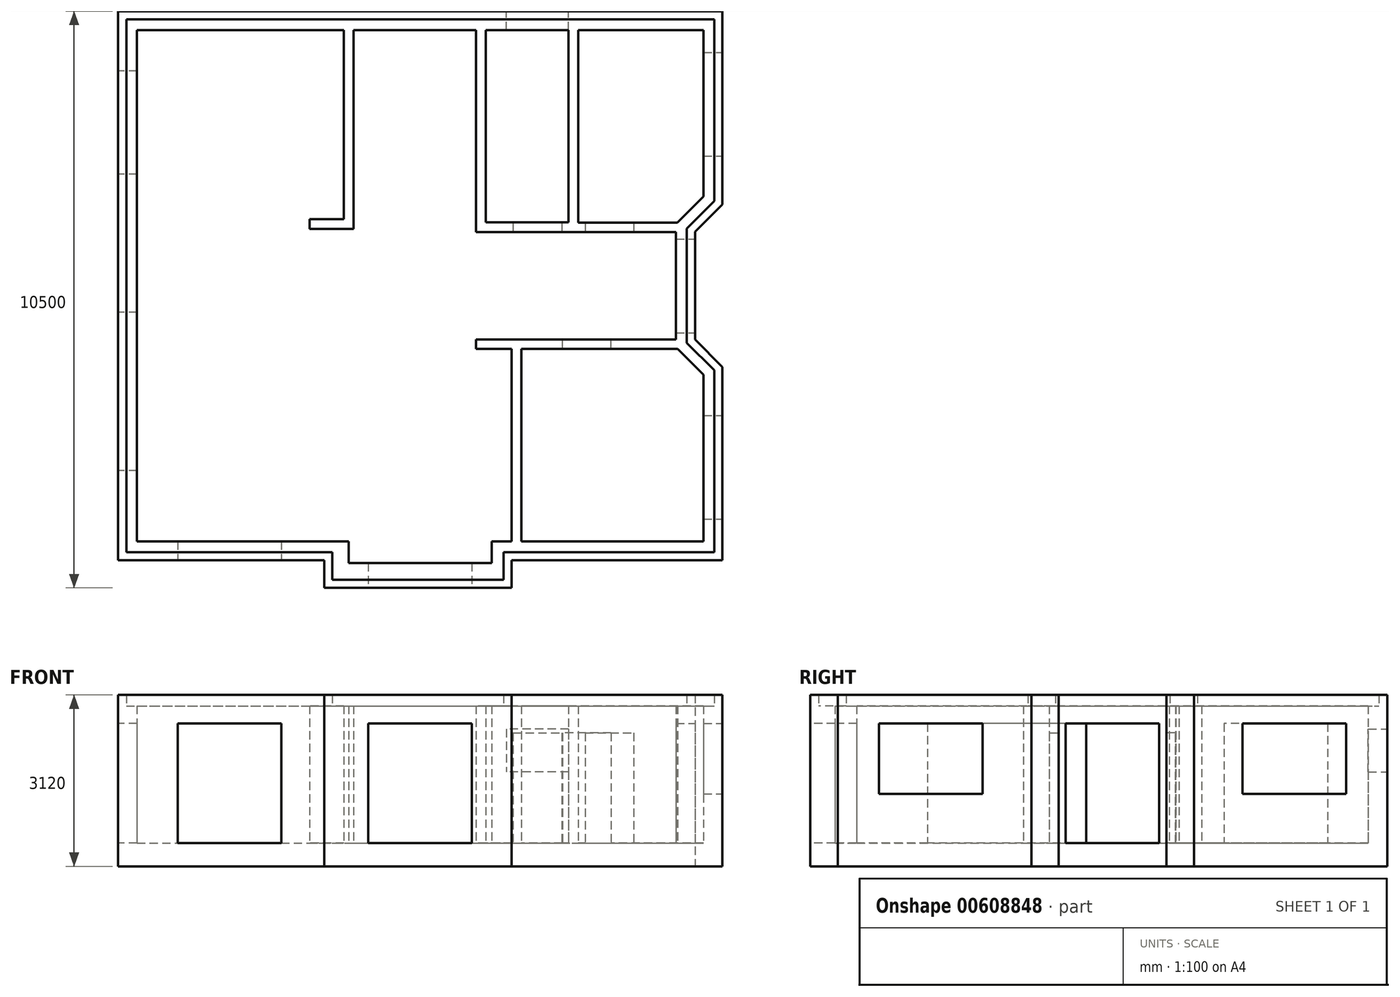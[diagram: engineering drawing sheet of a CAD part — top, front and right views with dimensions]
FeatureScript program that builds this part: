
annotation { "Feature Type Name" : "Feature", "Feature Type Description" : "" }
export const myFeature = defineFeature(function(context is Context, id is Id, definition is map)
    precondition{}
    {
        {
            var Q0;
            Q0=qCreatedBy(makeId("Top.planeOp"),FACE);
            var sketch = newSketch(context, id + "F0", { "sketchPlane" : qUnion([Q0])});
            skLineSegment(sketch, "E0.left", {"start": v(0, -10000) * mm, "end": v(0, 0) * mm});
            skLineSegment(sketch, "E1.bottom", {"start": v(345, -345) * mm, "end": v(4110, -345) * mm});
            skLineSegment(sketch, "E1.top", {"start": v(0, 0) * mm, "end": v(11000, 0) * mm});
            skLineSegment(sketch, "E2", {"start": v(345, -345) * mm, "end": v(345, -9655) * mm});
            skLineSegment(sketch, "E3", {"start": v(4110, -345) * mm, "end": v(4110, -3790) * mm});
            skLineSegment(sketch, "E4", {"start": v(4110, -3790) * mm, "end": v(3485, -3790) * mm});
            skLineSegment(sketch, "E5", {"start": v(3485, -3790) * mm, "end": v(3485, -3965) * mm});
            skLineSegment(sketch, "E6", {"start": v(3485, -3965) * mm, "end": v(4285, -3965) * mm});
            skLineSegment(sketch, "E7", {"start": v(4285, -3965) * mm, "end": v(4285, -345) * mm});
            skLineSegment(sketch, "E8.trimOffspring", {"start": v(4285, -345) * mm, "end": v(6515, -345) * mm});
            skLineSegment(sketch, "E9", {"start": v(6515, -345) * mm, "end": v(6515, -4020) * mm});
            skLineSegment(sketch, "E10", {"start": v(6515, -4020) * mm, "end": v(10155, -4020) * mm});
            skLineSegment(sketch, "E11", {"start": v(8200, -3845) * mm, "end": v(6690, -3845) * mm});
            skLineSegment(sketch, "E12", {"start": v(6690, -3845) * mm, "end": v(6690, -345) * mm});
            skLineSegment(sketch, "E13.trimOffspring", {"start": v(6690, -345) * mm, "end": v(8200, -345) * mm});
            skLineSegment(sketch, "E14", {"start": v(0, -10000) * mm, "end": v(3750, -10000) * mm});
            skLineSegment(sketch, "E15", {"start": v(3750, -10000) * mm, "end": v(3750, -10500) * mm});
            skLineSegment(sketch, "E16", {"start": v(3750, -10500) * mm, "end": v(7165, -10500) * mm});
            skLineSegment(sketch, "E17", {"start": v(7165, -10500) * mm, "end": v(7165, -10000) * mm});
            skLineSegment(sketch, "E18", {"start": v(7165, -10000) * mm, "end": v(11000, -10000) * mm});
            skLineSegment(sketch, "E19", {"start": v(11000, -10000) * mm, "end": v(11000, -6477.1) * mm});
            skLineSegment(sketch, "E20", {"start": v(10500, -5977.1) * mm, "end": v(10500, -4017.9) * mm});
            skLineSegment(sketch, "E21", {"start": v(10500, -4017.9) * mm, "end": v(11000, -3517.9) * mm});
            skLineSegment(sketch, "E22", {"start": v(11000, -3517.9) * mm, "end": v(11000, 0) * mm});
            skLineSegment(sketch, "E23", {"start": v(345, -9655) * mm, "end": v(4200, -9655) * mm});
            skLineSegment(sketch, "E24", {"start": v(4200, -9655) * mm, "end": v(4200, -10050) * mm});
            skLineSegment(sketch, "E25", {"start": v(4200, -10050) * mm, "end": v(6800, -10050) * mm});
            skLineSegment(sketch, "E26", {"start": v(6800, -10050) * mm, "end": v(6800, -9655) * mm});
            skLineSegment(sketch, "E27", {"start": v(6800, -9655) * mm, "end": v(7165, -9655) * mm});
            skLineSegment(sketch, "E28", {"start": v(10655, -9655) * mm, "end": v(10655, -6620) * mm});
            skLineSegment(sketch, "E29", {"start": v(10655, -6620) * mm, "end": v(10185, -6150) * mm});
            skLineSegment(sketch, "E30", {"start": v(10180, -3850) * mm, "end": v(10655, -3375) * mm});
            skLineSegment(sketch, "E31", {"start": v(10655, -3375) * mm, "end": v(10655, -345) * mm});
            skLineSegment(sketch, "E32", {"start": v(10185, -6150) * mm, "end": v(7340, -6150) * mm});
            skLineSegment(sketch, "E33", {"start": v(7340, -6150) * mm, "end": v(7340, -9655) * mm});
            skLineSegment(sketch, "E34", {"start": v(7165, -9655) * mm, "end": v(7165, -6150) * mm});
            skLineSegment(sketch, "E35", {"start": v(7165, -6150) * mm, "end": v(6515, -6150) * mm});
            skLineSegment(sketch, "E36", {"start": v(6515, -6150) * mm, "end": v(6515, -5975) * mm});
            skLineSegment(sketch, "E37", {"start": v(6515, -5975) * mm, "end": v(10155, -5975) * mm});
            skLineSegment(sketch, "E38", {"start": v(10155, -5975) * mm, "end": v(10155, -4020) * mm});
            skLineSegment(sketch, "E39.trimOffspring", {"start": v(7340, -9655) * mm, "end": v(10655, -9655) * mm});
            skLineSegment(sketch, "E40", {"start": v(10180, -3850) * mm, "end": v(8375, -3850) * mm});
            skLineSegment(sketch, "E41", {"start": v(8375, -3850) * mm, "end": v(8375, -345) * mm});
            skLineSegment(sketch, "E42", {"start": v(8200, -345) * mm, "end": v(8200, -3845) * mm});
            skLineSegment(sketch, "E43.trimOffspring", {"start": v(8375, -345) * mm, "end": v(10655, -345) * mm});
            skLineSegment(sketch, "E44", {"start": v(10500, -5977.1) * mm, "end": v(11000, -6477.1) * mm});
            skSolve(sketch);
        }
        {
            var Q0;
            Q0=makeQuery(id+"F0.imprint","IMPRINT",FACE,{"disambiguationData":[TD([[makeQuery(id+"F0.imprint","IMPRINT",EDGE,{"derivedFrom":sQuery(id+"F0.wireOp",EDGE,"E0.left")}),-1.0]])]});
            extrude(context, id + "F1", {"entities" : qUnion([Q0]), "depth" : 2500 * mm, "offsetDistance" : 25 * mm});
        }
        {
            var Q0;
            Q0=makeQuery(id+"F1.opExtrude","CAP_FACE",FACE,{"disambiguationData":[OSD([sQuery(id+"F0.wireOp",EDGE,"E0.left"),sQuery(id+"F0.wireOp",EDGE,"E1.bottom"),sQuery(id+"F0.wireOp",EDGE,"E1.top"),sQuery(id+"F0.wireOp",EDGE,"E2"),sQuery(id+"F0.wireOp",EDGE,"E3"),sQuery(id+"F0.wireOp",EDGE,"E4"),sQuery(id+"F0.wireOp",EDGE,"E5"),sQuery(id+"F0.wireOp",EDGE,"E6"),sQuery(id+"F0.wireOp",EDGE,"E7"),sQuery(id+"F0.wireOp",EDGE,"E8.trimOffspring"),sQuery(id+"F0.wireOp",EDGE,"E9"),sQuery(id+"F0.wireOp",EDGE,"E10"),sQuery(id+"F0.wireOp",EDGE,"E11"),sQuery(id+"F0.wireOp",EDGE,"E12"),sQuery(id+"F0.wireOp",EDGE,"E13.trimOffspring"),sQuery(id+"F0.wireOp",EDGE,"E14"),sQuery(id+"F0.wireOp",EDGE,"E15"),sQuery(id+"F0.wireOp",EDGE,"E16"),sQuery(id+"F0.wireOp",EDGE,"E17"),sQuery(id+"F0.wireOp",EDGE,"E18"),sQuery(id+"F0.wireOp",EDGE,"E19"),sQuery(id+"F0.wireOp",EDGE,"E20"),sQuery(id+"F0.wireOp",EDGE,"E21"),sQuery(id+"F0.wireOp",EDGE,"E22"),sQuery(id+"F0.wireOp",EDGE,"E23"),sQuery(id+"F0.wireOp",EDGE,"E24"),sQuery(id+"F0.wireOp",EDGE,"E25"),sQuery(id+"F0.wireOp",EDGE,"E26"),sQuery(id+"F0.wireOp",EDGE,"E27"),sQuery(id+"F0.wireOp",EDGE,"E28"),sQuery(id+"F0.wireOp",EDGE,"E29"),sQuery(id+"F0.wireOp",EDGE,"E30"),sQuery(id+"F0.wireOp",EDGE,"E31"),sQuery(id+"F0.wireOp",EDGE,"E32"),sQuery(id+"F0.wireOp",EDGE,"E33"),sQuery(id+"F0.wireOp",EDGE,"E34"),sQuery(id+"F0.wireOp",EDGE,"E35"),sQuery(id+"F0.wireOp",EDGE,"E36"),sQuery(id+"F0.wireOp",EDGE,"E37"),sQuery(id+"F0.wireOp",EDGE,"E38"),sQuery(id+"F0.wireOp",EDGE,"E39.trimOffspring"),sQuery(id+"F0.wireOp",EDGE,"E40"),sQuery(id+"F0.wireOp",EDGE,"E41"),sQuery(id+"F0.wireOp",EDGE,"E42"),sQuery(id+"F0.wireOp",EDGE,"E43.trimOffspring"),sQuery(id+"F0.wireOp",EDGE,"E44")])],"isStart":true});
            var sketch = newSketch(context, id + "F2", { "sketchPlane" : qUnion([Q0])});
            skLineSegment(sketch, "E45.0", {"start": v(0, 10000) * mm, "end": v(0, 0) * mm});
            skLineSegment(sketch, "E46.0", {"start": v(0, 0) * mm, "end": v(11000, 0) * mm});
            skLineSegment(sketch, "E47.0", {"start": v(11000, 3517.9) * mm, "end": v(11000, 0) * mm});
            skLineSegment(sketch, "E48.0", {"start": v(10500, 4017.9) * mm, "end": v(11000, 3517.9) * mm});
            skLineSegment(sketch, "E49.0", {"start": v(10500, 5977.1) * mm, "end": v(10500, 4017.9) * mm});
            skLineSegment(sketch, "E50.0", {"start": v(10500, 5977.1) * mm, "end": v(11000, 6477.1) * mm});
            skLineSegment(sketch, "E51.0", {"start": v(11000, 10000) * mm, "end": v(11000, 6477.1) * mm});
            skLineSegment(sketch, "E52.0", {"start": v(7165, 10000) * mm, "end": v(11000, 10000) * mm});
            skLineSegment(sketch, "E53.0", {"start": v(7165, 10500) * mm, "end": v(7165, 10000) * mm});
            skLineSegment(sketch, "E54.0", {"start": v(3750, 10500) * mm, "end": v(7165, 10500) * mm});
            skLineSegment(sketch, "E55.0", {"start": v(3750, 10000) * mm, "end": v(3750, 10500) * mm});
            skLineSegment(sketch, "E56.0", {"start": v(0, 10000) * mm, "end": v(3750, 10000) * mm});
            skSolve(sketch);
        }
        {
            var Q0;
            Q0 = qSketchRegion(id + "F2", true);
            extrude(context, id + "F3", {"entities" : qUnion([Q0]), "operationType" : NewBodyOperationType.ADD, "depth" : (250 + 170) * mm, "offsetDistance" : 25 * mm});
        }
        {
            var Q0;
            Q0=makeQuery(id+"F3.boolean.opBoolean","MERGE",FACE,{"derivedFrom":[makeQuery(id+"F1.opExtrude","SWEPT_FACE",FACE,{"disambiguationData":[OSD([sQuery(id+"F0.wireOp",EDGE,"E20")])]}),makeQuery(id+"F3.opExtrude","SWEPT_FACE",FACE,{"disambiguationData":[OSD([sQuery(id+"F2.wireOp",EDGE,"E49.0")])]})]});
            var sketch = newSketch(context, id + "F4", { "sketchPlane" : qUnion([Q0])});
            skLineSegment(sketch, "E57.bottom", {"start": v(-5855, 2180) * mm, "end": v(-4150, 2180) * mm});
            skLineSegment(sketch, "E57.top", {"start": v(-5855, 0) * mm, "end": v(-4150, 0) * mm});
            skLineSegment(sketch, "E57.left", {"start": v(-5855, 2180) * mm, "end": v(-5855, 0) * mm});
            skLineSegment(sketch, "E57.right", {"start": v(-4150, 2180) * mm, "end": v(-4150, 0) * mm});
            skSolve(sketch);
        }
        {
            var Q0;
            Q0 = qSketchRegion(id + "F4", true);
            extrude(context, id + "F5", {"entities" : qUnion([Q0]), "operationType" : NewBodyOperationType.REMOVE, "endBound" : BoundingType.UP_TO_NEXT, "oppositeDirection" : true, "depth" : 25 * mm, "offsetDistance" : 25 * mm});
        }
        {
            var Q0;
            Q0=makeQuery(id+"F1.opExtrude","SWEPT_FACE",FACE,{"disambiguationData":[OSD([sQuery(id+"F0.wireOp",EDGE,"E10")])]});
            var sketch = newSketch(context, id + "F6", { "sketchPlane" : qUnion([Q0])});
            skLineSegment(sketch, "E58.bottom", {"start": v(7190, 2010) * mm, "end": v(8075, 2010) * mm});
            skLineSegment(sketch, "E58.top", {"start": v(7190, 0) * mm, "end": v(8075, 0) * mm});
            skLineSegment(sketch, "E58.left", {"start": v(7190, 2010) * mm, "end": v(7190, 0) * mm});
            skLineSegment(sketch, "E58.right", {"start": v(8075, 2010) * mm, "end": v(8075, 0) * mm});
            skLineSegment(sketch, "E59.bottom", {"start": v(8500, 2010) * mm, "end": v(9385, 2010) * mm});
            skLineSegment(sketch, "E59.top", {"start": v(8500, 0) * mm, "end": v(9385, 0) * mm});
            skLineSegment(sketch, "E59.left", {"start": v(8500, 2010) * mm, "end": v(8500, 0) * mm});
            skLineSegment(sketch, "E59.right", {"start": v(9385, 2010) * mm, "end": v(9385, 0) * mm});
            skSolve(sketch);
        }
        {
            var Q0;
            Q0 = qSketchRegion(id + "F6", true);
            extrude(context, id + "F7", {"entities" : qUnion([Q0]), "operationType" : NewBodyOperationType.REMOVE, "endBound" : BoundingType.UP_TO_NEXT, "oppositeDirection" : true, "depth" : 25 * mm, "offsetDistance" : 25 * mm});
        }
        {
            var Q0;
            Q0=makeQuery(id+"F1.opExtrude","SWEPT_FACE",FACE,{"disambiguationData":[OSD([sQuery(id+"F0.wireOp",EDGE,"E37")])]});
            var sketch = newSketch(context, id + "F8", { "sketchPlane" : qUnion([Q0])});
            skLineSegment(sketch, "E60.bottom", {"start": v(-8975, 2010) * mm, "end": v(-8090, 2010) * mm});
            skLineSegment(sketch, "E60.top", {"start": v(-8975, 0) * mm, "end": v(-8090, 0) * mm});
            skLineSegment(sketch, "E60.left", {"start": v(-8975, 2010) * mm, "end": v(-8975, 0) * mm});
            skLineSegment(sketch, "E60.right", {"start": v(-8090, 2010) * mm, "end": v(-8090, 0) * mm});
            skSolve(sketch);
        }
        {
            var Q0;
            Q0 = qSketchRegion(id + "F8", true);
            extrude(context, id + "F9", {"entities" : qUnion([Q0]), "operationType" : NewBodyOperationType.REMOVE, "endBound" : BoundingType.UP_TO_NEXT, "oppositeDirection" : true, "depth" : 25 * mm, "offsetDistance" : 25 * mm});
        }
        {
            var Q0;
            Q0=makeQuery(id+"F3.boolean.opBoolean","MERGE",FACE,{"derivedFrom":[makeQuery(id+"F1.opExtrude","SWEPT_FACE",FACE,{"disambiguationData":[OSD([sQuery(id+"F0.wireOp",EDGE,"E0.left")])]}),makeQuery(id+"F3.opExtrude","SWEPT_FACE",FACE,{"disambiguationData":[OSD([sQuery(id+"F2.wireOp",EDGE,"E45.0")])]})]});
            var sketch = newSketch(context, id + "F10", { "sketchPlane" : qUnion([Q0])});
            skLineSegment(sketch, "E61.bottom", {"start": v(1085, 2180) * mm, "end": v(2970, 2180) * mm});
            skLineSegment(sketch, "E61.top", {"start": v(1085, 0) * mm, "end": v(2970, 0) * mm});
            skLineSegment(sketch, "E61.left", {"start": v(1085, 2180) * mm, "end": v(1085, 0) * mm});
            skLineSegment(sketch, "E61.right", {"start": v(2970, 2180) * mm, "end": v(2970, 0) * mm});
            skLineSegment(sketch, "E62.bottom", {"start": v(5480, 2180) * mm, "end": v(8365, 2180) * mm});
            skLineSegment(sketch, "E62.top", {"start": v(5480, 0) * mm, "end": v(8365, 0) * mm});
            skLineSegment(sketch, "E62.left", {"start": v(5480, 2180) * mm, "end": v(5480, 0) * mm});
            skLineSegment(sketch, "E62.right", {"start": v(8365, 2180) * mm, "end": v(8365, 0) * mm});
            skSolve(sketch);
        }
        {
            var Q0;
            Q0 = qSketchRegion(id + "F10", true);
            extrude(context, id + "F11", {"entities" : qUnion([Q0]), "operationType" : NewBodyOperationType.REMOVE, "endBound" : BoundingType.UP_TO_NEXT, "oppositeDirection" : true, "depth" : 25 * mm, "offsetDistance" : 25 * mm});
        }
        {
            var Q0;
            Q0=makeQuery(id+"F3.boolean.opBoolean","MERGE",FACE,{"derivedFrom":[makeQuery(id+"F1.opExtrude","SWEPT_FACE",FACE,{"disambiguationData":[OSD([sQuery(id+"F0.wireOp",EDGE,"E14")])]}),makeQuery(id+"F3.opExtrude","SWEPT_FACE",FACE,{"disambiguationData":[OSD([sQuery(id+"F2.wireOp",EDGE,"E56.0")])]})]});
            var sketch = newSketch(context, id + "F12", { "sketchPlane" : qUnion([Q0])});
            skLineSegment(sketch, "E63.bottom", {"start": v(1085, 2180) * mm, "end": v(2970, 2180) * mm});
            skLineSegment(sketch, "E63.top", {"start": v(1085, 0) * mm, "end": v(2970, 0) * mm});
            skLineSegment(sketch, "E63.left", {"start": v(1085, 2180) * mm, "end": v(1085, 0) * mm});
            skLineSegment(sketch, "E63.right", {"start": v(2970, 2180) * mm, "end": v(2970, 0) * mm});
            skSolve(sketch);
        }
        {
            var Q0;
            Q0=makeQuery(id+"F12.imprint","IMPRINT",FACE,{"disambiguationData":[TD([[makeQuery(id+"F12.imprint","IMPRINT",EDGE,{"derivedFrom":sQuery(id+"F12.wireOp",EDGE,"E63.bottom")}),-1.0]])]});
            extrude(context, id + "F13", {"entities" : qUnion([Q0]), "operationType" : NewBodyOperationType.REMOVE, "endBound" : BoundingType.UP_TO_NEXT, "oppositeDirection" : true, "depth" : 25 * mm, "offsetDistance" : 25 * mm});
        }
        {
            var Q0;
            Q0=makeQuery(id+"F3.boolean.opBoolean","MERGE",FACE,{"derivedFrom":[makeQuery(id+"F1.opExtrude","SWEPT_FACE",FACE,{"disambiguationData":[OSD([sQuery(id+"F0.wireOp",EDGE,"E16")])]}),makeQuery(id+"F3.opExtrude","SWEPT_FACE",FACE,{"disambiguationData":[OSD([sQuery(id+"F2.wireOp",EDGE,"E54.0")])]})]});
            var sketch = newSketch(context, id + "F14", { "sketchPlane" : qUnion([Q0])});
            skLineSegment(sketch, "E64.bottom", {"start": v(4555, 2180) * mm, "end": v(6440, 2180) * mm});
            skLineSegment(sketch, "E64.top", {"start": v(4555, 0) * mm, "end": v(6440, 0) * mm});
            skLineSegment(sketch, "E64.left", {"start": v(4555, 2180) * mm, "end": v(4555, 0) * mm});
            skLineSegment(sketch, "E64.right", {"start": v(6440, 2180) * mm, "end": v(6440, 0) * mm});
            skSolve(sketch);
        }
        {
            var Q0;
            Q0=makeQuery(id+"F14.imprint","IMPRINT",FACE,{"disambiguationData":[TD([[makeQuery(id+"F14.imprint","IMPRINT",EDGE,{"derivedFrom":sQuery(id+"F14.wireOp",EDGE,"E64.bottom")}),-1.0]])]});
            extrude(context, id + "F15", {"entities" : qUnion([Q0]), "operationType" : NewBodyOperationType.REMOVE, "endBound" : BoundingType.UP_TO_NEXT, "oppositeDirection" : true, "depth" : 25 * mm, "offsetDistance" : 25 * mm});
        }
        {
            var Q0;
            Q0=makeQuery(id+"F3.boolean.opBoolean","MERGE",FACE,{"derivedFrom":[makeQuery(id+"F1.opExtrude","SWEPT_FACE",FACE,{"disambiguationData":[OSD([sQuery(id+"F0.wireOp",EDGE,"E19")])]}),makeQuery(id+"F3.opExtrude","SWEPT_FACE",FACE,{"disambiguationData":[OSD([sQuery(id+"F2.wireOp",EDGE,"E51.0")])]})]});
            var sketch = newSketch(context, id + "F16", { "sketchPlane" : qUnion([Q0])});
            skLineSegment(sketch, "E65.bottom", {"start": v(-9250, 2180) * mm, "end": v(-7365, 2180) * mm});
            skLineSegment(sketch, "E65.top", {"start": v(-9250, 900) * mm, "end": v(-7365, 900) * mm});
            skLineSegment(sketch, "E65.left", {"start": v(-9250, 2180) * mm, "end": v(-9250, 900) * mm});
            skLineSegment(sketch, "E65.right", {"start": v(-7365, 2180) * mm, "end": v(-7365, 900) * mm});
            skLineSegment(sketch, "E66.bottom", {"start": v(-2635, 2180) * mm, "end": v(-750, 2180) * mm});
            skLineSegment(sketch, "E66.top", {"start": v(-2635, 900) * mm, "end": v(-750, 900) * mm});
            skLineSegment(sketch, "E66.left", {"start": v(-2635, 2180) * mm, "end": v(-2635, 900) * mm});
            skLineSegment(sketch, "E66.right", {"start": v(-750, 2180) * mm, "end": v(-750, 900) * mm});
            skSolve(sketch);
        }
        {
            var Q0;
            Q0=makeQuery(id+"F16.imprint","IMPRINT",FACE,{"disambiguationData":[TD([[makeQuery(id+"F16.imprint","IMPRINT",EDGE,{"derivedFrom":sQuery(id+"F16.wireOp",EDGE,"E65.bottom")}),-1.0]])]});
            var Q1;
            Q1=makeQuery(id+"F16.imprint","IMPRINT",FACE,{"disambiguationData":[TD([[makeQuery(id+"F16.imprint","IMPRINT",EDGE,{"derivedFrom":sQuery(id+"F16.wireOp",EDGE,"E66.bottom")}),-1.0]])]});
            extrude(context, id + "F17", {"entities" : qUnion([Q0, Q1]), "operationType" : NewBodyOperationType.REMOVE, "endBound" : BoundingType.UP_TO_NEXT, "oppositeDirection" : true, "depth" : 25 * mm, "offsetDistance" : 25 * mm});
        }
        {
            var Q0;
            Q0=makeQuery(id+"F3.boolean.opBoolean","MERGE",FACE,{"derivedFrom":[makeQuery(id+"F1.opExtrude","SWEPT_FACE",FACE,{"disambiguationData":[OSD([sQuery(id+"F0.wireOp",EDGE,"E1.top")])]}),makeQuery(id+"F3.opExtrude","SWEPT_FACE",FACE,{"disambiguationData":[OSD([sQuery(id+"F2.wireOp",EDGE,"E46.0")])]})]});
            var sketch = newSketch(context, id + "F18", { "sketchPlane" : qUnion([Q0])});
            skLineSegment(sketch, "E67.bottom", {"start": v(-8200, 2080) * mm, "end": v(-7070, 2080) * mm});
            skLineSegment(sketch, "E67.top", {"start": v(-8200, 1300) * mm, "end": v(-7070, 1300) * mm});
            skLineSegment(sketch, "E67.left", {"start": v(-8200, 2080) * mm, "end": v(-8200, 1300) * mm});
            skLineSegment(sketch, "E67.right", {"start": v(-7070, 2080) * mm, "end": v(-7070, 1300) * mm});
            skSolve(sketch);
        }
        {
            var Q0;
            Q0=makeQuery(id+"F18.imprint","IMPRINT",FACE,{"disambiguationData":[TD([[makeQuery(id+"F18.imprint","IMPRINT",EDGE,{"derivedFrom":sQuery(id+"F18.wireOp",EDGE,"E67.bottom")}),-1.0]])]});
            extrude(context, id + "F19", {"entities" : qUnion([Q0]), "operationType" : NewBodyOperationType.REMOVE, "endBound" : BoundingType.UP_TO_NEXT, "oppositeDirection" : true, "depth" : 25 * mm, "offsetDistance" : 25 * mm});
        }
        {
            var Q0;
            Q0=makeQuery(id+"F1.opExtrude","CAP_FACE",FACE,{"disambiguationData":[OSD([sQuery(id+"F0.wireOp",EDGE,"E0.left"),sQuery(id+"F0.wireOp",EDGE,"E1.bottom"),sQuery(id+"F0.wireOp",EDGE,"E1.top"),sQuery(id+"F0.wireOp",EDGE,"E2"),sQuery(id+"F0.wireOp",EDGE,"E3"),sQuery(id+"F0.wireOp",EDGE,"E4"),sQuery(id+"F0.wireOp",EDGE,"E5"),sQuery(id+"F0.wireOp",EDGE,"E6"),sQuery(id+"F0.wireOp",EDGE,"E7"),sQuery(id+"F0.wireOp",EDGE,"E8.trimOffspring"),sQuery(id+"F0.wireOp",EDGE,"E9"),sQuery(id+"F0.wireOp",EDGE,"E10"),sQuery(id+"F0.wireOp",EDGE,"E11"),sQuery(id+"F0.wireOp",EDGE,"E12"),sQuery(id+"F0.wireOp",EDGE,"E13.trimOffspring"),sQuery(id+"F0.wireOp",EDGE,"E14"),sQuery(id+"F0.wireOp",EDGE,"E15"),sQuery(id+"F0.wireOp",EDGE,"E16"),sQuery(id+"F0.wireOp",EDGE,"E17"),sQuery(id+"F0.wireOp",EDGE,"E18"),sQuery(id+"F0.wireOp",EDGE,"E19"),sQuery(id+"F0.wireOp",EDGE,"E20"),sQuery(id+"F0.wireOp",EDGE,"E21"),sQuery(id+"F0.wireOp",EDGE,"E22"),sQuery(id+"F0.wireOp",EDGE,"E23"),sQuery(id+"F0.wireOp",EDGE,"E24"),sQuery(id+"F0.wireOp",EDGE,"E25"),sQuery(id+"F0.wireOp",EDGE,"E26"),sQuery(id+"F0.wireOp",EDGE,"E27"),sQuery(id+"F0.wireOp",EDGE,"E28"),sQuery(id+"F0.wireOp",EDGE,"E29"),sQuery(id+"F0.wireOp",EDGE,"E30"),sQuery(id+"F0.wireOp",EDGE,"E31"),sQuery(id+"F0.wireOp",EDGE,"E32"),sQuery(id+"F0.wireOp",EDGE,"E33"),sQuery(id+"F0.wireOp",EDGE,"E34"),sQuery(id+"F0.wireOp",EDGE,"E35"),sQuery(id+"F0.wireOp",EDGE,"E36"),sQuery(id+"F0.wireOp",EDGE,"E37"),sQuery(id+"F0.wireOp",EDGE,"E38"),sQuery(id+"F0.wireOp",EDGE,"E39.trimOffspring"),sQuery(id+"F0.wireOp",EDGE,"E40"),sQuery(id+"F0.wireOp",EDGE,"E41"),sQuery(id+"F0.wireOp",EDGE,"E42"),sQuery(id+"F0.wireOp",EDGE,"E43.trimOffspring"),sQuery(id+"F0.wireOp",EDGE,"E44")])],"isStart":false});
            var sketch = newSketch(context, id + "F20", { "sketchPlane" : qUnion([Q0])});
            skLineSegment(sketch, "E68.0", {"start": v(0, -10000) * mm, "end": v(0, 0) * mm});
            skLineSegment(sketch, "E69.0", {"start": v(0, 0) * mm, "end": v(11000, 0) * mm});
            skLineSegment(sketch, "E70.0", {"start": v(0, -10000) * mm, "end": v(3750, -10000) * mm});
            skLineSegment(sketch, "E71.0", {"start": v(3750, -10000) * mm, "end": v(3750, -10500) * mm});
            skLineSegment(sketch, "E72.0", {"start": v(3750, -10500) * mm, "end": v(7165, -10500) * mm});
            skLineSegment(sketch, "E73.0", {"start": v(11000, -10000) * mm, "end": v(11000, -6477.1) * mm});
            skLineSegment(sketch, "E73.1", {"start": v(7165, -10000) * mm, "end": v(11000, -10000) * mm});
            skLineSegment(sketch, "E73.2", {"start": v(7165, -10500) * mm, "end": v(7165, -10000) * mm});
            skLineSegment(sketch, "E74.0", {"start": v(10500, -5977.1) * mm, "end": v(11000, -6477.1) * mm});
            skLineSegment(sketch, "E75.0", {"start": v(10500, -5977.1) * mm, "end": v(10500, -4017.9) * mm});
            skLineSegment(sketch, "E76.0", {"start": v(10500, -4017.9) * mm, "end": v(11000, -3517.9) * mm});
            skLineSegment(sketch, "E77.0", {"start": v(11000, -3517.9) * mm, "end": v(11000, 0) * mm});
            skLineSegment(sketch, "E78.0", {"start": v(150, -9850) * mm, "end": v(3900, -9850) * mm});
            skLineSegment(sketch, "E78.1", {"start": v(10350, -6039.23) * mm, "end": v(10350, -3955.77) * mm});
            skLineSegment(sketch, "E78.2", {"start": v(10350, -3955.77) * mm, "end": v(10850, -3455.77) * mm});
            skLineSegment(sketch, "E78.3", {"start": v(10850, -3455.77) * mm, "end": v(10850, -150) * mm});
            skLineSegment(sketch, "E78.4", {"start": v(150, -150) * mm, "end": v(10850, -150) * mm});
            skLineSegment(sketch, "E78.5", {"start": v(10350, -6039.23) * mm, "end": v(10850, -6539.23) * mm});
            skLineSegment(sketch, "E78.6", {"start": v(150, -9850) * mm, "end": v(150, -150) * mm});
            skLineSegment(sketch, "E78.7", {"start": v(10850, -9850) * mm, "end": v(10850, -6539.23) * mm});
            skLineSegment(sketch, "E78.8", {"start": v(7015, -9850) * mm, "end": v(10850, -9850) * mm});
            skLineSegment(sketch, "E78.9", {"start": v(7015, -10350) * mm, "end": v(7015, -9850) * mm});
            skLineSegment(sketch, "E78.10", {"start": v(3900, -10350) * mm, "end": v(7015, -10350) * mm});
            skLineSegment(sketch, "E78.11", {"start": v(3900, -9850) * mm, "end": v(3900, -10350) * mm});
            skLineSegment(sketch, "E79", {"start": v(11000, -3517.9) * mm, "end": v(10655, -3375) * mm, "construction": true});
            skSolve(sketch);
        }
        {
            var Q0;
            Q0 = qSketchRegion(id + "F20", true);
            extrude(context, id + "F21", {"entities" : qUnion([Q0]), "operationType" : NewBodyOperationType.ADD, "depth" : 200 * mm, "offsetDistance" : 25 * mm});
        }
    });
